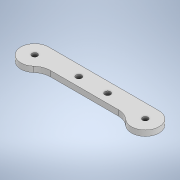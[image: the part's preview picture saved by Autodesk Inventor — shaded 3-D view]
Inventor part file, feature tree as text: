
AUTODESK INVENTOR PART (.ipt)
format: ipt  version: 2020 (Build 240168000, 168)  size: 141,824 bytes
history: native  units: in
note: dims shown in document units (in); Inventor stores cm internally (conversion verified against a paired STEP export)
features: extrude x1, fillet x1, sketch x1
ambient origin geometry x8: Origin, YZ Plane, XZ Plane, XY Plane, X Axis, Y Axis, Z Axis, Center Point
bodies: Solid1 (feature_tree)
feature tree (3):
  extrude  "Extrusion1"  Depth=0.3937in
  fillet  "Fillet1"  Radius=0.122in
  sketch  "Sketch1"  dims[d0=0.3937in d1=0.3937in d2=0.5906in d3=0.5906in d4=0.122in d5=0.122in d6=0.122in d7=0.1181in d8=0.0in d9=0.3937in d10=0.122in d11=0.122in]
